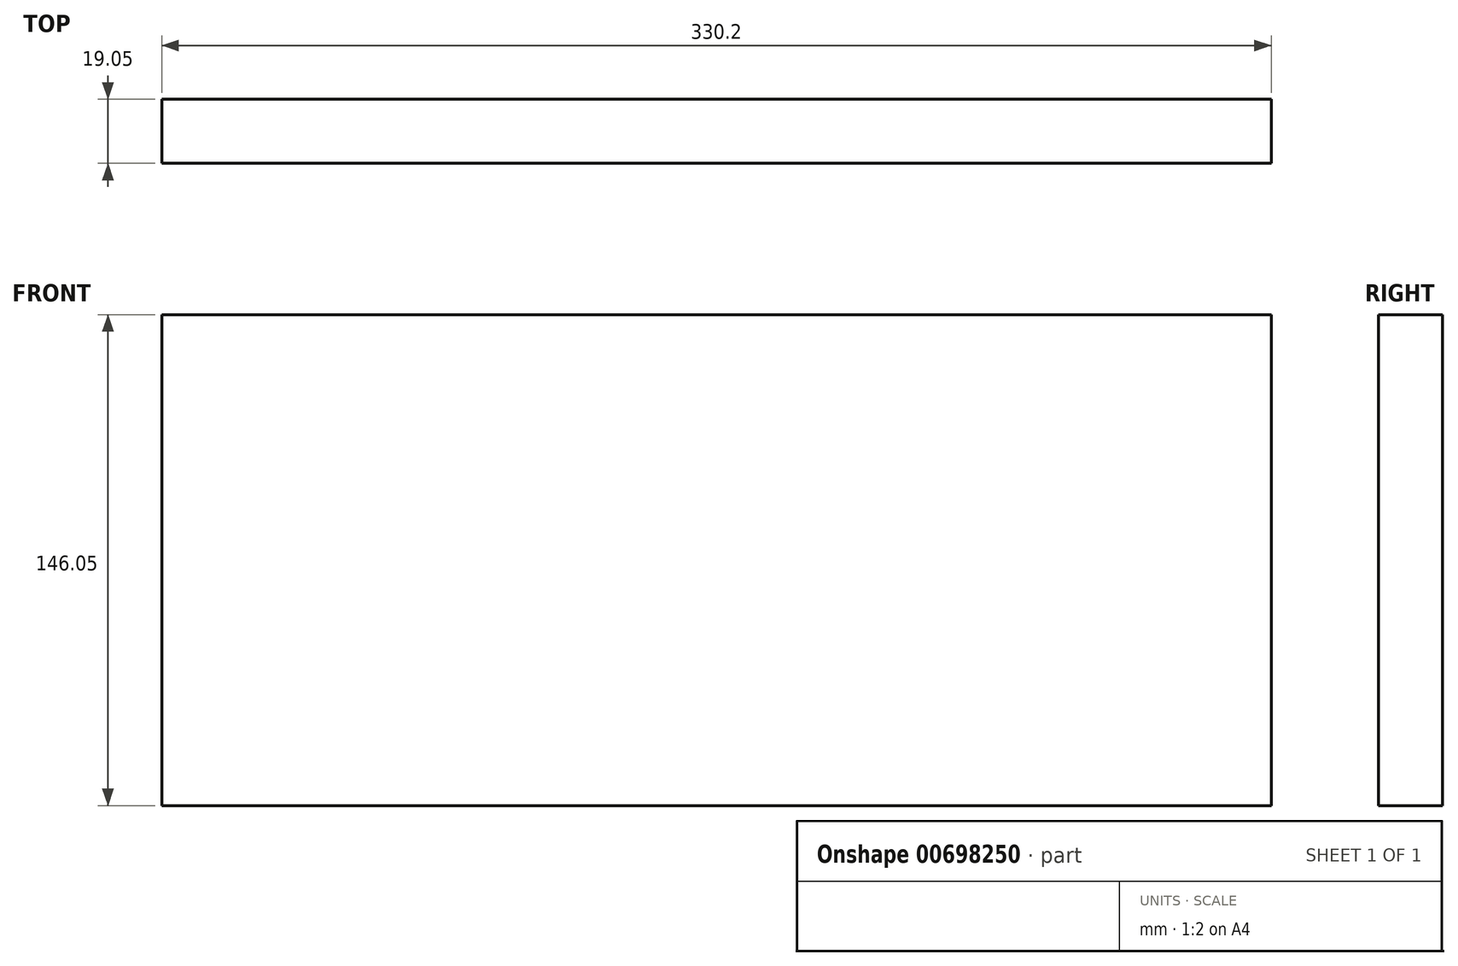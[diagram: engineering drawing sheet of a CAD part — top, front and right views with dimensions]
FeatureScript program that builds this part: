
annotation { "Feature Type Name" : "Feature", "Feature Type Description" : "" }
export const myFeature = defineFeature(function(context is Context, id is Id, definition is map)
    precondition{}
    {
        {
            var Q0;
            Q0=qCreatedBy(makeId("Front.planeOp"),FACE);
            var sketch = newSketch(context, id + "F0", { "sketchPlane" : qUnion([Q0])});
            skLineSegment(sketch, "E0.bottom", {"start": v(-206.26, -104.28) * mm, "end": v(123.94, -104.28) * mm});
            skLineSegment(sketch, "E0.top", {"start": v(-206.26, 41.77) * mm, "end": v(123.94, 41.77) * mm});
            skLineSegment(sketch, "E0.left", {"start": v(-206.26, -104.28) * mm, "end": v(-206.26, 41.77) * mm});
            skLineSegment(sketch, "E0.right", {"start": v(123.94, -104.28) * mm, "end": v(123.94, 41.77) * mm});
            skSolve(sketch);
        }
        {
            var Q0;
            Q0=makeQuery(id+"F0.imprint","IMPRINT",FACE,{"disambiguationData":[TD([[makeQuery(id+"F0.imprint","IMPRINT",EDGE,{"derivedFrom":sQuery(id+"F0.wireOp",EDGE,"E0.bottom")}),1.0]])]});
            extrude(context, id + "F1", {"entities" : qUnion([Q0]), "depth" : 19.05 * mm, "offsetDistance" : 25.4 * mm});
        }
    });
